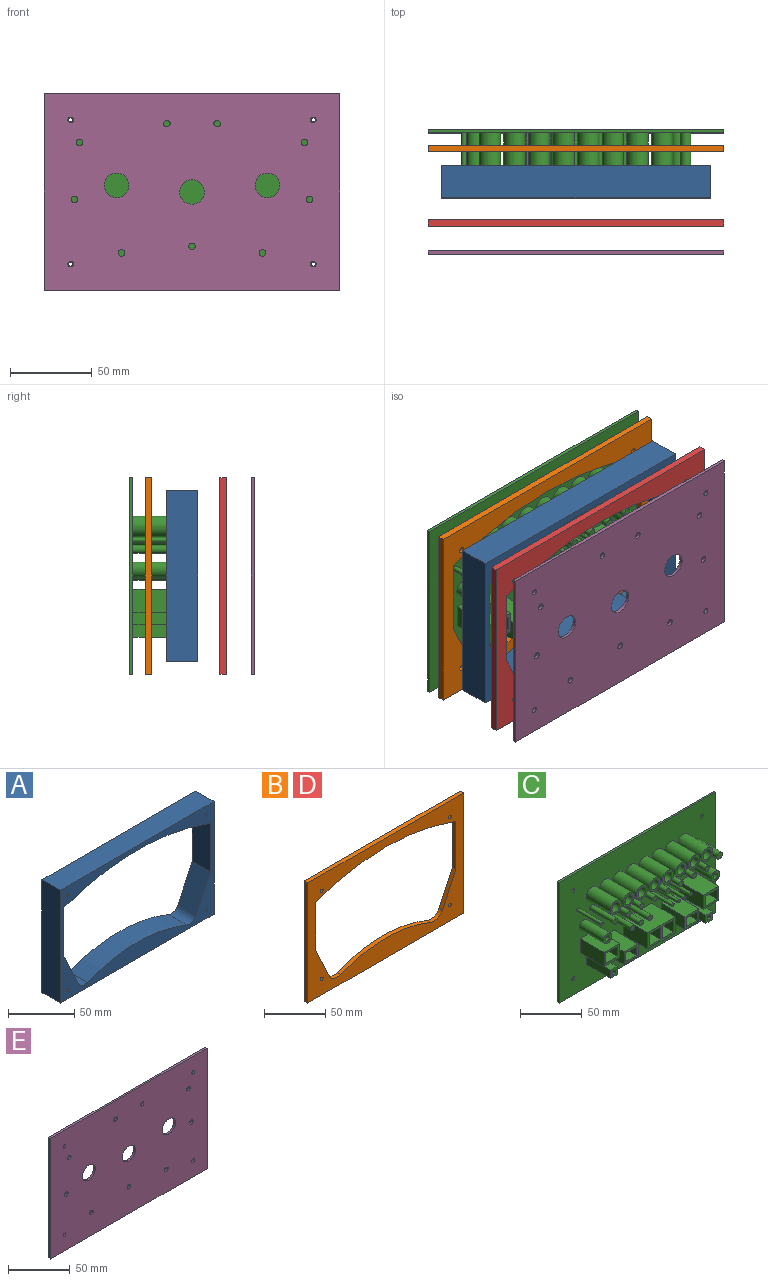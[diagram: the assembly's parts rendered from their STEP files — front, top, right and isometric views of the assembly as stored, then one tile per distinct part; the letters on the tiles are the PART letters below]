
ASSEMBLY  parts=5 mates=4
PART A: 18 faces, bbox 164x19.4x104 mm
  f0: plane 164x19.43mm, normal (0,0,1), area 3186.5mm2, adj f1,f11,f12,f13
  f1: plane 104x19.43mm, normal (-1,0,0), area 2020.7mm2, adj f0,f2,f12,f13
  f2: plane 164x19.43mm, normal (0,0,-1), area 3186.5mm2, adj f1,f11,f12,f13
  f3: plane 45.08x19.43mm, normal (1,0,0), area 875.8mm2, adj f4,f10,f12,f13
  f4: cylinder r=224mm len=156mm, axis (0,1,0), area 3095.9mm2, adj f3,f5,f12,f13
  f5: plane 45.08x19.43mm, normal (-1,0,0), area 875.8mm2, adj f4,f6,f12,f13
  f6: plane 32.77x19.43mm, normal (-0.91,0,0.42), area 702.6mm2, adj f5,f7,f12,f13
  f7: cylinder r=7.4mm len=19.43mm, axis (0,1,0), area 219.6mm2, adj f6,f8,f12,f13
  f8: cylinder r=139mm len=106.36mm, axis (0,1,0), area 2120.7mm2, adj f7,f9,f12,f13
  f9: cylinder r=7.4mm len=19.43mm, axis (0,1,0), area 219.6mm2, adj f8,f10,f12,f13
  f10: plane 32.77x19.43mm, normal (0.91,0,0.42), area 702.6mm2, adj f3,f9,f12,f13
  f11: plane 104x19.43mm, normal (1,0,0), area 2020.7mm2, adj f0,f2,f12,f13
  f12: plane 164x104mm, normal (0,-1,0), area 4222.6mm2, adj f0,f1,f2,f3,f4,f5,f6,f7
  f13: plane 164x104mm, normal (0,1,0), area 4222.6mm2, adj f0,f1,f2,f3,f4,f5,f6,f7
  f14: cylinder r=1.25mm len=19.43mm, axis (0,1,0), area 152.6mm2, adj f12,f13
  f15: cylinder r=1.25mm len=19.43mm, axis (0,1,0), area 152.6mm2, adj f12,f13
  f16: cylinder r=1.25mm len=19.43mm, axis (0,1,0), area 152.6mm2, adj f12,f13
  f17: cylinder r=1.25mm len=19.43mm, axis (0,1,0), area 152.6mm2, adj f12,f13
PART B: 18 faces, bbox 180x4x120 mm
  f0: plane 47.82x4mm, normal (1,0,0), area 191.3mm2, adj f1,f11,f12,f13
  f1: cylinder r=227mm len=162mm, axis (0,1,0), area 662.6mm2, adj f0,f2,f12,f13
  f2: plane 47.82x4mm, normal (-1,0,0), area 191.3mm2, adj f1,f3,f12,f13
  f3: plane 33.37x15.56mm, normal (-0.91,0,0.42), area 147.3mm2, adj f2,f4,f12,f13
  f4: cylinder r=10.4mm len=13.4mm, axis (0,1,0), area 63.5mm2, adj f3,f5,f12,f13
  f5: cylinder r=136mm len=104.07mm, axis (0,1,0), area 427.2mm2, adj f4,f6,f12,f13
  f6: cylinder r=10.4mm len=13.4mm, axis (0,1,0), area 63.5mm2, adj f5,f11,f12,f13
  f7: plane 120x4mm, normal (1,0,0), area 480mm2, adj f8,f10,f12,f13
  f8: plane 180x4mm, normal (0,0,1), area 720mm2, adj f7,f9,f12,f13
  f9: plane 120x4mm, normal (-1,0,0), area 480mm2, adj f8,f10,f12,f13
  f10: plane 180x4mm, normal (0,0,-1), area 720mm2, adj f7,f9,f12,f13
  f11: plane 33.37x15.56mm, normal (0.91,0,0.42), area 147.3mm2, adj f0,f6,f12,f13
  f12: plane 180x120mm, normal (0,-1,0), area 7359.4mm2, adj f0,f1,f2,f3,f4,f5,f6,f7
  f13: plane 180x120mm, normal (0,1,0), area 7359.4mm2, adj f0,f1,f2,f3,f4,f5,f6,f7
  f14: cylinder r=1.7mm len=4mm, axis (0,1,0), area 42.7mm2, adj f12,f13
  f15: cylinder r=1.7mm len=4mm, axis (0,1,0), area 42.7mm2, adj f12,f13
  f16: cylinder r=1.7mm len=4mm, axis (0,1,0), area 42.7mm2, adj f12,f13
  f17: cylinder r=1.7mm len=4mm, axis (0,1,0), area 42.7mm2, adj f12,f13
PART C: 141 faces, bbox 180x29.4x120 mm
  f0: plane 180x120mm, normal (0,-1,0), area 18540.3mm2, adj f25,f26,f27,f45,f48,f49,f50,f51
  f1: plane 29.43x10mm, normal (-1,0,0), area 294.3mm2, adj f2,f46,f47,f116
  f2: plane 29.43x14mm, normal (0,0,1), area 412mm2, adj f1,f3,f47,f116
  f3: plane 29.43x10mm, normal (1,0,0), area 294.3mm2, adj f2,f46,f47,f116
  f4: plane 29.43x13mm, normal (0,0,-1), area 382.6mm2, adj f5,f28,f47,f106
  f5: plane 29.43x12mm, normal (-1,0,0), area 353.2mm2, adj f4,f6,f47,f106
  f6: plane 29.43x13mm, normal (0,0,1), area 382.6mm2, adj f5,f28,f47,f106
  f7: plane 29.43x13mm, normal (0,0,1), area 382.6mm2, adj f8,f29,f47,f106
  f8: plane 29.43x12mm, normal (1,0,0), area 353.2mm2, adj f7,f9,f47,f106
  f9: plane 29.43x13mm, normal (0,0,-1), area 382.6mm2, adj f8,f29,f47,f106
  f10: plane 29.43x8.5mm, normal (-1,0,0), area 250.2mm2, adj f11,f30,f47,f135
  f11: plane 29.43x12mm, normal (0,0,1), area 353.2mm2, adj f10,f12,f47,f135
  f12: plane 29.43x8.5mm, normal (1,0,0), area 250.2mm2, adj f11,f30,f47,f135
  f13: plane 29.43x14mm, normal (0,0,-1), area 412mm2, adj f14,f31,f47,f140
  f14: plane 29.43x10mm, normal (-1,0,0), area 294.3mm2, adj f13,f15,f47,f140
  f15: plane 29.43x14mm, normal (0,0,1), area 412mm2, adj f14,f31,f47,f140
  f16: plane 29.43x3.5mm, normal (0,0,-1), area 103mm2, adj f17,f42,f47,f130
  f17: plane 29.43x4mm, normal (-1,0,0), area 117.7mm2, adj f16,f18,f47,f130
  f18: plane 29.43x3.5mm, normal (0,0,1), area 103mm2, adj f17,f42,f47,f130
  f19: plane 29.43x3.5mm, normal (0,0,-1), area 103mm2, adj f20,f43,f47,f121
  f20: plane 29.43x4mm, normal (-1,0,0), area 117.7mm2, adj f19,f21,f47,f121
  f21: plane 29.43x3.5mm, normal (0,0,1), area 103mm2, adj f20,f43,f47,f121
  f22: plane 29.43x8.5mm, normal (-1,0,0), area 250.2mm2, adj f23,f44,f47,f111
  f23: plane 29.43x12mm, normal (0,0,1), area 353.2mm2, adj f22,f24,f47,f111
  f24: plane 29.43x8.5mm, normal (1,0,0), area 250.2mm2, adj f23,f44,f47,f111
  f25: plane 120x2mm, normal (1,0,0), area 240mm2, adj f0,f26,f45,f47
  f26: plane 180x2mm, normal (0,0,1), area 360mm2, adj f0,f25,f27,f47
  f27: plane 120x2mm, normal (-1,0,0), area 240mm2, adj f0,f26,f45,f47
  f28: plane 29.43x12mm, normal (1,0,0), area 353.2mm2, adj f4,f6,f47,f106
  f29: plane 29.43x12mm, normal (-1,0,0), area 353.2mm2, adj f7,f9,f47,f106
  f30: plane 29.43x12mm, normal (0,0,-1), area 353.2mm2, adj f10,f12,f47,f135
  f31: plane 29.43x10mm, normal (1,0,0), area 294.3mm2, adj f13,f15,f47,f140
  f32: cylinder r=2.76mm len=29.43mm, axis (0,-1,0), area 510.8mm2, adj f47,f125
  f33: cylinder r=2.76mm len=29.43mm, axis (0,-1,0), area 510.8mm2, adj f47,f69
  f34: cylinder r=4.5mm len=29.43mm, axis (0,-1,0), area 832.1mm2, adj f47,f67
  f35: cylinder r=4.5mm len=29.43mm, axis (0,-1,0), area 832.1mm2, adj f47,f65
  f36: cylinder r=4.5mm len=29.43mm, axis (0,-1,0), area 832.1mm2, adj f47,f63
  f37: cylinder r=4.5mm len=29.43mm, axis (0,-1,0), area 832.1mm2, adj f47,f61
  f38: cylinder r=4.5mm len=29.43mm, axis (0,-1,0), area 832.1mm2, adj f47,f59
  f39: cylinder r=4.5mm len=29.43mm, axis (0,-1,0), area 832.1mm2, adj f47,f57
  f40: cylinder r=4.5mm len=29.43mm, axis (0,-1,0), area 832.1mm2, adj f47,f55
  f41: cylinder r=4.5mm len=29.43mm, axis (0,-1,0), area 832.1mm2, adj f47,f53
  f42: plane 29.43x4mm, normal (1,0,0), area 117.7mm2, adj f16,f18,f47,f130
  f43: plane 29.43x4mm, normal (1,0,0), area 117.7mm2, adj f19,f21,f47,f121
  f44: plane 29.43x12mm, normal (0,0,-1), area 353.2mm2, adj f22,f24,f47,f111
  f45: plane 180x2mm, normal (0,0,-1), area 360mm2, adj f0,f25,f27,f47
  f46: plane 29.43x14mm, normal (0,0,-1), area 412mm2, adj f1,f3,f47,f116
  f47: plane 180x120mm, normal (0,1,0), area 20182.8mm2, adj f1,f2,f3,f4,f5,f6,f7,f8
  f48: cylinder r=1.7mm len=3.4mm, axis (0,-1,0), area 21.4mm2, adj f0,f47
  f49: cylinder r=1.7mm len=3.4mm, axis (0,-1,0), area 21.4mm2, adj f0,f47
  f50: cylinder r=1.7mm len=3.4mm, axis (0,-1,0), area 21.4mm2, adj f0,f47
  f51: cylinder r=1.7mm len=3.4mm, axis (0,-1,0), area 21.4mm2, adj f0,f47
  f52: cylinder r=6.5mm len=27.43mm, axis (0,1,0), area 1120.3mm2, adj f0,f53
  f53: plane 13x13mm, normal (0,-1,0), area 69.1mm2, adj f41,f52
  f54: cylinder r=6.5mm len=27.43mm, axis (0,1,0), area 1120.3mm2, adj f0,f55
  f55: plane 13x13mm, normal (0,-1,0), area 69.1mm2, adj f40,f54
  f56: cylinder r=6.5mm len=27.43mm, axis (0,1,0), area 1120.3mm2, adj f0,f57
  f57: plane 13x13mm, normal (0,-1,0), area 69.1mm2, adj f39,f56
  f58: cylinder r=6.5mm len=27.43mm, axis (0,1,0), area 1120.3mm2, adj f0,f59
  f59: plane 13x13mm, normal (0,-1,0), area 69.1mm2, adj f38,f58
  f60: cylinder r=6.5mm len=27.43mm, axis (0,1,0), area 1120.3mm2, adj f0,f61
  f61: plane 13x13mm, normal (0,-1,0), area 69.1mm2, adj f37,f60
  f62: cylinder r=6.5mm len=27.43mm, axis (0,1,0), area 1120.3mm2, adj f0,f63
  f63: plane 13x13mm, normal (0,-1,0), area 69.1mm2, adj f36,f62
  f64: cylinder r=6.5mm len=27.43mm, axis (0,1,0), area 1120.3mm2, adj f0,f65
  f65: plane 13x13mm, normal (0,-1,0), area 69.1mm2, adj f35,f64
  f66: cylinder r=6.5mm len=27.43mm, axis (0,1,0), area 1120.3mm2, adj f0,f67
  f67: plane 13x13mm, normal (0,-1,0), area 69.1mm2, adj f34,f66
  f68: cylinder r=4.76mm len=27.43mm, axis (0,1,0), area 820.8mm2, adj f0,f69
  f69: plane 9.53x9.53mm, normal (0,-1,0), area 47.3mm2, adj f33,f68
  f70: cylinder r=2.5mm len=27.43mm, axis (0,1,0), area 430.9mm2, adj f0,f71
  f71: plane 5x5mm, normal (0,-1,0), area 19.6mm2, adj f70
  f72: cylinder r=2.5mm len=27.43mm, axis (0,1,0), area 430.9mm2, adj f0,f73
  f73: plane 5x5mm, normal (0,-1,0), area 19.6mm2, adj f72
  f74: cylinder r=2.5mm len=27.43mm, axis (0,1,0), area 430.9mm2, adj f0,f75
  f75: plane 5x5mm, normal (0,-1,0), area 19.6mm2, adj f74
  f76: cylinder r=1.5mm len=27.43mm, axis (0,1,0), area 258.5mm2, adj f0,f77
  f77: plane 3x3mm, normal (0,-1,0), area 7.1mm2, adj f76
  f78: cylinder r=1.5mm len=27.43mm, axis (0,1,0), area 258.5mm2, adj f0,f79
  f79: plane 3x3mm, normal (0,-1,0), area 7.1mm2, adj f78
  f80: cylinder r=1.5mm len=27.43mm, axis (0,1,0), area 258.5mm2, adj f0,f81
  f81: plane 3x3mm, normal (0,-1,0), area 7.1mm2, adj f80
  f82: cylinder r=1.5mm len=27.43mm, axis (0,1,0), area 258.5mm2, adj f0,f83
  f83: plane 3x3mm, normal (0,-1,0), area 7.1mm2, adj f82
  f84: cylinder r=1.5mm len=27.43mm, axis (0,1,0), area 258.5mm2, adj f0,f85
  f85: plane 3x3mm, normal (0,-1,0), area 7.1mm2, adj f84
  f86: cylinder r=2.5mm len=27.43mm, axis (0,1,0), area 430.9mm2, adj f0,f87
  f87: plane 5x5mm, normal (0,-1,0), area 19.6mm2, adj f86
  f88: cylinder r=2.5mm len=27.43mm, axis (0,1,0), area 430.9mm2, adj f0,f89
  f89: plane 5x5mm, normal (0,-1,0), area 19.6mm2, adj f88
  f90: cylinder r=2.5mm len=27.43mm, axis (0,1,0), area 430.9mm2, adj f0,f91
  f91: plane 5x5mm, normal (0,-1,0), area 19.6mm2, adj f90
  f92: cylinder r=2.5mm len=27.43mm, axis (0,1,0), area 430.9mm2, adj f0,f93
  f93: plane 5x5mm, normal (0,-1,0), area 19.6mm2, adj f92
  f94: cylinder r=2.5mm len=27.43mm, axis (0,1,0), area 430.9mm2, adj f0,f95
  f95: plane 5x5mm, normal (0,-1,0), area 19.6mm2, adj f94
  f96: cylinder r=2.5mm len=27.43mm, axis (0,1,0), area 430.9mm2, adj f0,f97
  f97: plane 5x5mm, normal (0,-1,0), area 19.6mm2, adj f96
  f98: cylinder r=2.5mm len=27.43mm, axis (0,1,0), area 430.9mm2, adj f0,f99
  f99: plane 5x5mm, normal (0,-1,0), area 19.6mm2, adj f98
  f100: cylinder r=2.5mm len=27.43mm, axis (0,1,0), area 430.9mm2, adj f0,f101
  f101: plane 5x5mm, normal (0,-1,0), area 19.6mm2, adj f100
  f102: plane 27.43x16mm, normal (-1,0,0), area 438.9mm2, adj f0,f103,f105,f106
  f103: plane 32x27.43mm, normal (0,0,-1), area 877.8mm2, adj f0,f102,f104,f106
  f104: plane 27.43x16mm, normal (1,0,0), area 438.9mm2, adj f0,f103,f105,f106
  f105: plane 32x27.43mm, normal (0,0,1), area 877.8mm2, adj f0,f102,f104,f106
  f106: plane 32x16mm, normal (0,-1,0), area 200mm2, adj f4,f5,f6,f7,f8,f9,f28,f29
  f107: plane 27.43x12.5mm, normal (-1,0,0), area 342.9mm2, adj f0,f108,f110,f111
  f108: plane 27.43x16mm, normal (0,0,-1), area 438.9mm2, adj f0,f107,f109,f111
  f109: plane 27.43x12.5mm, normal (1,0,0), area 342.9mm2, adj f0,f108,f110,f111
  f110: plane 27.43x16mm, normal (0,0,1), area 438.9mm2, adj f0,f107,f109,f111
  f111: plane 16x12.5mm, normal (0,-1,0), area 98mm2, adj f22,f23,f24,f44,f107,f108,f109,f110
  f112: plane 27.43x18mm, normal (0,0,1), area 493.7mm2, adj f0,f113,f115,f116
  f113: plane 27.43x14mm, normal (-1,0,0), area 384mm2, adj f0,f112,f114,f116
  f114: plane 27.43x18mm, normal (0,0,-1), area 493.7mm2, adj f0,f113,f115,f116
  f115: plane 27.43x14mm, normal (1,0,0), area 384mm2, adj f0,f112,f114,f116
  f116: plane 18x14mm, normal (0,-1,0), area 112mm2, adj f1,f2,f3,f46,f112,f113,f114,f115
  f117: plane 27.43x7.5mm, normal (0,0,1), area 205.7mm2, adj f0,f118,f120,f121
  f118: plane 27.43x8mm, normal (-1,0,0), area 219.4mm2, adj f0,f117,f119,f121
  f119: plane 27.43x7.5mm, normal (0,0,-1), area 205.7mm2, adj f0,f118,f120,f121
  f120: plane 27.43x8mm, normal (1,0,0), area 219.4mm2, adj f0,f117,f119,f121
  f121: plane 8x7.5mm, normal (0,-1,0), area 46mm2, adj f19,f20,f21,f43,f117,f118,f119,f120
  f122: cylinder r=3.17mm len=27.43mm, axis (0,1,0), area 547.2mm2, adj f0,f123
  f123: plane 6.35x6.35mm, normal (0,-1,0), area 31.7mm2, adj f122
  f124: cylinder r=4.76mm len=27.43mm, axis (0,1,0), area 820.8mm2, adj f0,f125
  f125: plane 9.53x9.53mm, normal (0,-1,0), area 47.3mm2, adj f32,f124
  f126: plane 27.43x8mm, normal (1,0,0), area 219.4mm2, adj f0,f127,f129,f130
  f127: plane 27.43x7.5mm, normal (0,0,1), area 205.7mm2, adj f0,f126,f128,f130
  f128: plane 27.43x8mm, normal (-1,0,0), area 219.4mm2, adj f0,f127,f129,f130
  f129: plane 27.43x7.5mm, normal (0,0,-1), area 205.7mm2, adj f0,f126,f128,f130
  f130: plane 8x7.5mm, normal (0,-1,0), area 46mm2, adj f16,f17,f18,f42,f126,f127,f128,f129
  f131: plane 27.43x16mm, normal (0,0,-1), area 438.9mm2, adj f0,f132,f134,f135
  f132: plane 27.43x12.5mm, normal (1,0,0), area 342.9mm2, adj f0,f131,f133,f135
  f133: plane 27.43x16mm, normal (0,0,1), area 438.9mm2, adj f0,f132,f134,f135
  f134: plane 27.43x12.5mm, normal (-1,0,0), area 342.9mm2, adj f0,f131,f133,f135
  f135: plane 16x12.5mm, normal (0,-1,0), area 98mm2, adj f10,f11,f12,f30,f131,f132,f133,f134
  f136: plane 27.43x18mm, normal (0,0,-1), area 493.7mm2, adj f0,f137,f139,f140
  f137: plane 27.43x14mm, normal (1,0,0), area 384mm2, adj f0,f136,f138,f140
  f138: plane 27.43x18mm, normal (0,0,1), area 493.7mm2, adj f0,f137,f139,f140
  f139: plane 27.43x14mm, normal (-1,0,0), area 384mm2, adj f0,f136,f138,f140
  f140: plane 18x14mm, normal (0,-1,0), area 112mm2, adj f13,f14,f15,f31,f136,f137,f138,f139
PART D: same geometry as B
PART E: 22 faces, bbox 180x2x120 mm
  f0: plane 120x2mm, normal (1,0,0), area 240mm2, adj f1,f14,f16,f17
  f1: plane 180x2mm, normal (0,0,1), area 360mm2, adj f0,f2,f16,f17
  f2: plane 120x2mm, normal (-1,0,0), area 240mm2, adj f1,f14,f16,f17
  f3: cylinder r=7.5mm len=15mm, axis (0,1,0), area 94.2mm2, adj f16,f17
  f4: cylinder r=2mm len=4mm, axis (0,1,0), area 25.1mm2, adj f16,f17
  f5: cylinder r=2mm len=4mm, axis (0,1,0), area 25.1mm2, adj f16,f17
  f6: cylinder r=2mm len=4mm, axis (0,1,0), area 25.1mm2, adj f16,f17
  f7: cylinder r=2mm len=4mm, axis (0,1,0), area 25.1mm2, adj f16,f17
  f8: cylinder r=2mm len=4mm, axis (0,1,0), area 25.1mm2, adj f16,f17
  f9: cylinder r=2mm len=4mm, axis (0,1,0), area 25.1mm2, adj f16,f17
  f10: cylinder r=2mm len=4mm, axis (0,1,0), area 25.1mm2, adj f16,f17
  f11: cylinder r=2mm len=4mm, axis (0,1,0), area 25.1mm2, adj f16,f17
  f12: cylinder r=2mm len=4mm, axis (0,1,0), area 25.1mm2, adj f16,f17
  f13: cylinder r=7.5mm len=15mm, axis (0,1,0), area 94.2mm2, adj f16,f17
  f14: plane 180x2mm, normal (0,0,-1), area 360mm2, adj f0,f2,f16,f17
  f15: cylinder r=7.5mm len=15mm, axis (0,1,0), area 94.2mm2, adj f16,f17
  f16: plane 180x120mm, normal (0,-1,0), area 20920.4mm2, adj f0,f1,f2,f3,f4,f5,f6,f7
  f17: plane 180x120mm, normal (0,1,0), area 20920.4mm2, adj f0,f1,f2,f3,f4,f5,f6,f7
  f18: cylinder r=1.7mm len=3.4mm, axis (0,1,0), area 21.4mm2, adj f16,f17
  f19: cylinder r=1.7mm len=3.4mm, axis (0,1,0), area 21.4mm2, adj f16,f17
  f20: cylinder r=1.7mm len=3.4mm, axis (0,1,0), area 21.4mm2, adj f16,f17
  f21: cylinder r=1.7mm len=3.4mm, axis (0,1,0), area 21.4mm2, adj f16,f17
PLACE A t=(-271.83,190.26,-83.31)mm
PLACE B t=(-271.83,103,-83.31)mm
PLACE C t=(-271.83,10.55,-83.31)mm
PLACE D t=(-271.83,57.48,-83.31)mm
PLACE E t=(-271.83,338.4,-83.31)mm
MATE slider C.f48 <-> A.f14  axis (0,-1,0) through (-345.83,110.55,-39.31)mm
MATE slider C.f48 <-> E.f18  axis (0,-1,0) through (-345.83,110.55,-39.31)mm
MATE slider B.f14 <-> C.f48  axis (0,-1,0) through (-345.83,99,-39.31)mm
MATE slider C.f48 <-> D.f14  axis (0,-1,0) through (-345.83,110.55,-39.31)mm
